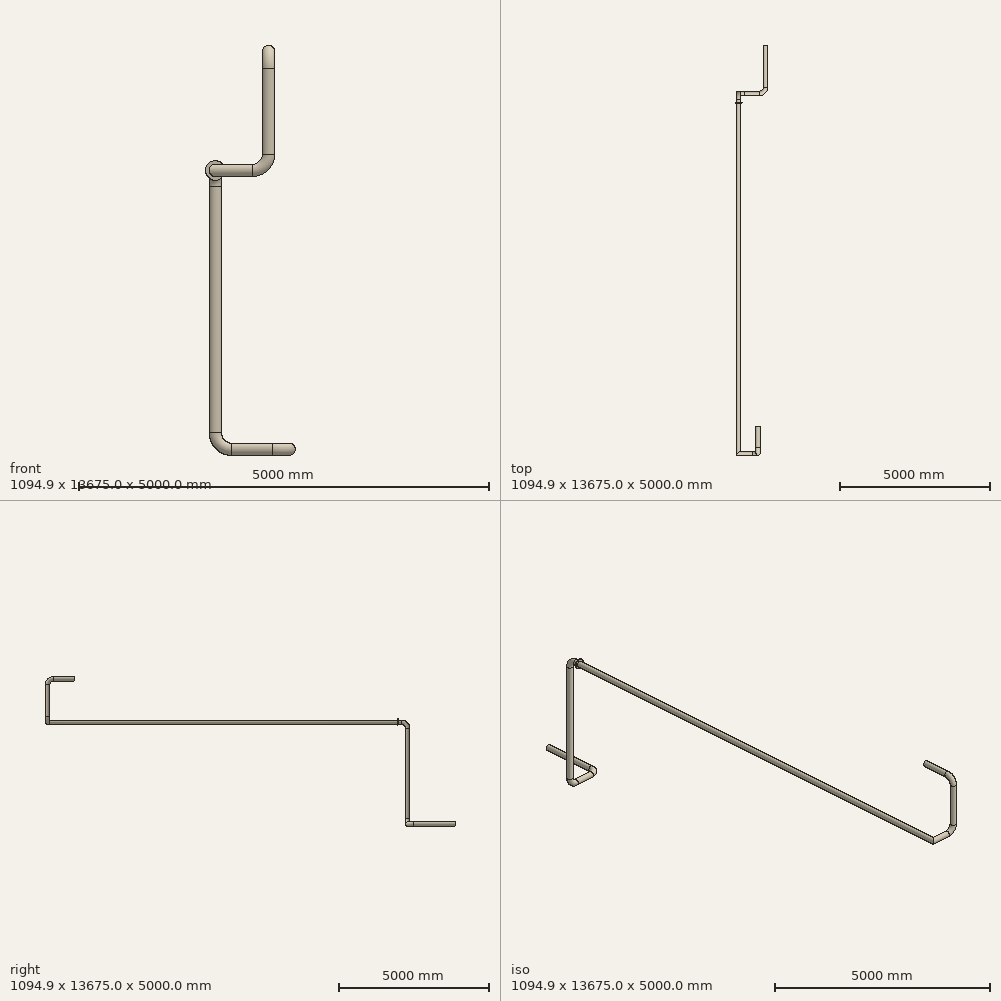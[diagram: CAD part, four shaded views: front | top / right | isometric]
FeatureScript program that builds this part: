
annotation { "Feature Type Name" : "Feature", "Feature Type Description" : "" }
export const myFeature = defineFeature(function(context is Context, id is Id, definition is map)
    precondition{}
    {
        {
            var Q0;
            Q0=qCreatedBy(makeId("Front.planeOp"),FACE);
            var sketch = newSketch(context, id + "F0", { "sketchPlane" : qUnion([Q0])});
            skCircle(sketch, "E0", {"center": v(0, 0) * mm, "radius": 75 * mm});
            skSolve(sketch);
        }
        {
            var Q0;
            Q0=qCreatedBy(makeId("Right.planeOp"),FACE);
            var sketch = newSketch(context, id + "F1", { "sketchPlane" : qUnion([Q0])});
            skLineSegment(sketch, "E1", {"start": v(0, 0) * mm, "end": v(-1600, 0) * mm});
            skSolve(sketch);
        }
        {
            var Q0;
            Q0=qCreatedBy(makeId("Top.planeOp"),FACE);
            var sketch = newSketch(context, id + "F2", { "sketchPlane" : qUnion([Q0])});
            skLineSegment(sketch, "E2.0", {"start": v(0, 0) * mm, "end": v(0, -1400) * mm});
            skLineSegment(sketch, "E3", {"start": v(-200, -1600) * mm, "end": v(-900, -1600) * mm});
            skPoint(sketch, "E4.visualSharp", {"position": v(0, -1600) * mm});
            skArc(sketch, "E4.filletArc", {"start": v(-200, -1600) * mm, "mid": v(-58.58, -1541.42) * mm, "end": v(0, -1400) * mm});
            skSolve(sketch);
        }
        {
            var Q0;
            Q0=qCreatedBy(makeId("Front.planeOp"),FACE);
            cPlane(context, id + "F3", {"entities" : qUnion([Q0]), "cplaneType" : CPlaneType.OFFSET, "offset" : 1600 * mm, "width" : 150 * mm, "height" : 150 * mm});
        }
        {
            var Q0;
            Q0=qCreatedBy(id+"F3.planeOp",FACE);
            var sketch = newSketch(context, id + "F4", { "sketchPlane" : qUnion([Q0])});
            skLineSegment(sketch, "E5.0", {"start": v(-200, 0) * mm, "end": v(-700, 0) * mm});
            skLineSegment(sketch, "E6", {"start": v(-900, 200) * mm, "end": v(-900, 3400) * mm});
            skPoint(sketch, "E7.visualSharp", {"position": v(-900, 0) * mm});
            skArc(sketch, "E7.filletArc", {"start": v(-900, 200) * mm, "mid": v(-841.42, 58.58) * mm, "end": v(-700, 0) * mm});
            skSolve(sketch);
        }
        {
            var Q0;
            Q0=qCreatedBy(makeId("Right.planeOp"),FACE);
            cPlane(context, id + "F5", {"entities" : qUnion([Q0]), "cplaneType" : CPlaneType.OFFSET, "offset" : 900 * mm, "oppositeDirection" : true, "width" : 150 * mm, "height" : 150 * mm});
        }
        {
            var Q0;
            Q0=qCreatedBy(id+"F5.planeOp",FACE);
            var sketch = newSketch(context, id + "F6", { "sketchPlane" : qUnion([Q0])});
            skLineSegment(sketch, "E8.0", {"start": v(-1600, 200) * mm, "end": v(-1600, 3200) * mm});
            skLineSegment(sketch, "E9", {"start": v(-1800, 3400) * mm, "end": v(-13600, 3400) * mm});
            skPoint(sketch, "E10.visualSharp", {"position": v(-1600, 3400) * mm});
            skArc(sketch, "E10.filletArc", {"start": v(-1600, 3200) * mm, "mid": v(-1658.58, 3341.42) * mm, "end": v(-1800, 3400) * mm});
            skSolve(sketch);
        }
        {
            var Q0;
            Q0=qCreatedBy(id+"F3.planeOp",FACE);
            cPlane(context, id + "F7", {"entities" : qUnion([Q0]), "cplaneType" : CPlaneType.OFFSET, "offset" : 12000 * mm, "width" : 150 * mm, "height" : 150 * mm});
        }
        {
            var Q0;
            Q0=qCreatedBy(id+"F7.planeOp",FACE);
            var sketch = newSketch(context, id + "F8", { "sketchPlane" : qUnion([Q0])});
            skLineSegment(sketch, "E11.0", {"start": v(-900, 3400) * mm, "end": v(-450, 3400) * mm});
            skPoint(sketch, "E12.visualSharp", {"position": v(-200, 3400) * mm});
            skArc(sketch, "E12.filletArc", {"start": v(-450, 3400) * mm, "mid": v(-308.58, 3458.58) * mm, "end": v(-250, 3600) * mm});
            skLineSegment(sketch, "E13", {"start": v(-250, 3600) * mm, "end": v(-250, 4850) * mm});
            skSolve(sketch);
        }
        {
            var Q0;
            Q0=qCreatedBy(makeId("Right.planeOp"),FACE);
            cPlane(context, id + "F9", {"entities" : qUnion([Q0]), "cplaneType" : CPlaneType.OFFSET, "offset" : 200 * mm, "oppositeDirection" : true, "width" : 150 * mm, "height" : 150 * mm});
        }
        {
            var Q0;
            Q0=qCreatedBy(makeId("Front.planeOp"),FACE);
            cPlane(context, id + "F10", {"entities" : qUnion([Q0]), "cplaneType" : CPlaneType.OFFSET, "offset" : (1600 + 300) * mm, "width" : 150 * mm, "height" : 150 * mm});
        }
        {
            var Q0;
            Q0=qCreatedBy(id+"F9.planeOp",FACE);
            cPlane(context, id + "F11", {"entities" : qUnion([Q0]), "cplaneType" : CPlaneType.OFFSET, "offset" : 50 * mm, "oppositeDirection" : true, "width" : 150 * mm, "height" : 150 * mm});
        }
        {
            var Q0;
            Q0=qCreatedBy(id+"F11.planeOp",FACE);
            var sketch = newSketch(context, id + "F12", { "sketchPlane" : qUnion([Q0])});
            skLineSegment(sketch, "E14.0", {"start": v(-13600, 3600) * mm, "end": v(-13600, 4650) * mm});
            skLineSegment(sketch, "E15", {"start": v(-13400, 4850) * mm, "end": v(-12700, 4850) * mm});
            skPoint(sketch, "E16.visualSharp", {"position": v(-13600, 4850) * mm});
            skArc(sketch, "E16.filletArc", {"start": v(-13400, 4850) * mm, "mid": v(-13541.42, 4791.42) * mm, "end": v(-13600, 4650) * mm});
            skSolve(sketch);
        }
        {
            var Q0;
            Q0=makeQuery(id+"F0.imprint","IMPRINT",FACE,{"disambiguationData":[TD([[makeQuery(id+"F0.imprint","IMPRINT",EDGE,{"derivedFrom":sQuery(id+"F0.wireOp",EDGE,"E0")}),1.0]])]});
            var Q1;
            Q1=sQuery(id+"F2.wireOp",EDGE,"E2.0");
            var Q2;
            Q2=sQuery(id+"F2.wireOp",EDGE,"E4.filletArc");
            var Q3;
            Q3=sQuery(id+"F4.wireOp",EDGE,"E5.0");
            var Q4;
            Q4=sQuery(id+"F4.wireOp",EDGE,"E7.filletArc");
            var Q5;
            Q5=sQuery(id+"F6.wireOp",EDGE,"E8.0");
            var Q6;
            Q6=sQuery(id+"F6.wireOp",EDGE,"E10.filletArc");
            var Q7;
            Q7=sQuery(id+"F6.wireOp",EDGE,"E9");
            var Q8;
            Q8=sQuery(id+"F8.wireOp",EDGE,"E11.0");
            var Q9;
            Q9=sQuery(id+"F8.wireOp",EDGE,"E12.filletArc");
            var Q10;
            Q10=sQuery(id+"F12.wireOp",EDGE,"E14.0");
            var Q11;
            Q11=sQuery(id+"F12.wireOp",EDGE,"E16.filletArc");
            var Q12;
            Q12=sQuery(id+"F12.wireOp",EDGE,"E15");
            sweep(context, id + "F13", {"profiles" : qUnion([Q0]), "path" : qUnion([Q1, Q2, Q3, Q4, Q5, Q6, Q7, Q8, Q9, Q10, Q11, Q12])});
        }
        {
            var Q0;
            Q0=qCreatedBy(id+"F10.planeOp",FACE);
            var sketch = newSketch(context, id + "F14", { "sketchPlane" : qUnion([Q0])});
            skCircle(sketch, "E17", {"center": v(-899.92, 3399.85) * mm, "radius": 120 * mm});
            skSolve(sketch);
        }
        {
            var Q0;
            Q0=makeQuery(id+"F14.imprint","IMPRINT",FACE,{"disambiguationData":[TD([[makeQuery(id+"F14.imprint","IMPRINT",EDGE,{"derivedFrom":sQuery(id+"F14.wireOp",EDGE,"E17")}),1.0]])]});
            extrude(context, id + "F15", {"entities" : qUnion([Q0]), "operationType" : NewBodyOperationType.ADD, "depth" : 25 * mm, "offsetDistance" : 25 * mm});
        }
    });
